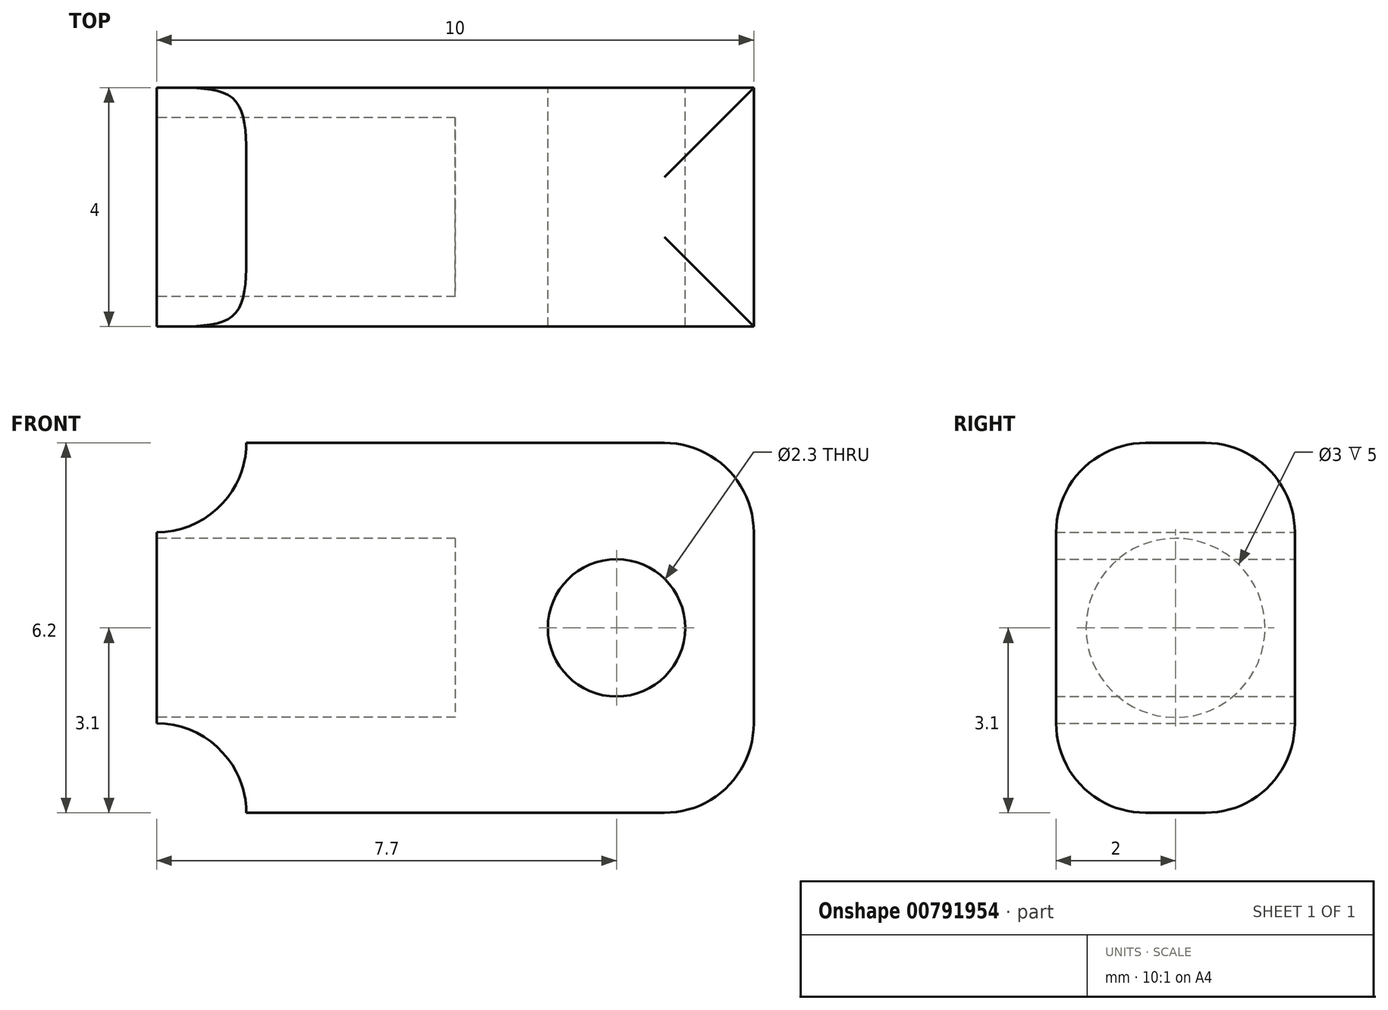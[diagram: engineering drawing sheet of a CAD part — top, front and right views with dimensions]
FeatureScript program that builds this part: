
annotation { "Feature Type Name" : "Feature", "Feature Type Description" : "" }
export const myFeature = defineFeature(function(context is Context, id is Id, definition is map)
    precondition{}
    {
        {
            var Q0;
            Q0=qCreatedBy(makeId("Front.planeOp"),FACE);
            var sketch = newSketch(context, id + "F0", { "sketchPlane" : qUnion([Q0])});
            skLineSegment(sketch, "E0.bottom", {"start": v(5, 3.1) * mm, "end": v(-3.5, 3.1) * mm});
            skLineSegment(sketch, "E0.top", {"start": v(5, -3.1) * mm, "end": v(-3.5, -3.1) * mm});
            skLineSegment(sketch, "E0.left", {"start": v(5, 3.1) * mm, "end": v(5, -3.1) * mm});
            skLineSegment(sketch, "E0.right", {"start": v(-5, 1.6) * mm, "end": v(-5, -1.6) * mm});
            skPoint(sketch, "E0.middle", {"position": v(0, 0) * mm});
            skArc(sketch, "E1", {"start": v(-5, 1.6) * mm, "mid": v(-3.94, 2.04) * mm, "end": v(-3.5, 3.1) * mm});
            skArc(sketch, "E2.MirrorCS", {"start": v(-5, -1.6) * mm, "mid": v(-3.94, -2.04) * mm, "end": v(-3.5, -3.1) * mm});
            skCircle(sketch, "E3", {"center": v(2.7, 0) * mm, "radius": 1.15 * mm});
            skSolve(sketch);
        }
        {
            var Q0;
            Q0 = qSketchRegion(id + "F0", true);
            extrude(context, id + "F1", {"entities" : qUnion([Q0]), "depth" : 4 * mm, "offsetDistance" : 25 * mm});
        }
        {
            var Q0;
            Q0=makeQuery(id+"F1.opExtrude","SWEPT_FACE",FACE,{"disambiguationData":[OSD([sQuery(id+"F0.wireOp",EDGE,"E0.right")])]});
            var sketch = newSketch(context, id + "F2", { "sketchPlane" : qUnion([Q0])});
            skCircle(sketch, "E4", {"center": v(2, 0) * mm, "radius": 1.5 * mm});
            skPoint(sketch, "E4.centerSnap0", {"position": v(2, 1.6) * mm});
            skSolve(sketch);
        }
        {
            var Q0;
            Q0 = qSketchRegion(id + "F2", true);
            extrude(context, id + "F3", {"entities" : qUnion([Q0]), "operationType" : NewBodyOperationType.REMOVE, "oppositeDirection" : true, "depth" : 5 * mm, "offsetDistance" : 25 * mm});
        }
        {
            var Q0;
            Q0=makeQuery(id+"F1.opExtrude","CAP_EDGE",EDGE,{"disambiguationData":[OSD([sQuery(id+"F0.wireOp",EDGE,"E0.bottom")])],"isStart":false});
            var Q1;
            Q1=makeQuery(id+"F1.opExtrude","CAP_EDGE",EDGE,{"disambiguationData":[OSD([sQuery(id+"F0.wireOp",EDGE,"E0.bottom")])],"isStart":true});
            var Q2;
            Q2=makeQuery(id+"F1.opExtrude","CAP_EDGE",EDGE,{"disambiguationData":[OSD([sQuery(id+"F0.wireOp",EDGE,"E0.top")])],"isStart":true});
            var Q3;
            Q3=makeQuery(id+"F1.opExtrude","CAP_EDGE",EDGE,{"disambiguationData":[OSD([sQuery(id+"F0.wireOp",EDGE,"E0.top")])],"isStart":false});
            var Q4;
            Q4=makeQuery(id+"F1.opExtrude","SWEPT_EDGE",EDGE,{"disambiguationData":[OSD([sQuery(id+"F0.wireOp",EDGE,"E0.top"),sQuery(id+"F0.wireOp",EDGE,"E0.left")])]});
            var Q5;
            Q5=makeQuery(id+"F1.opExtrude","SWEPT_EDGE",EDGE,{"disambiguationData":[OSD([sQuery(id+"F0.wireOp",EDGE,"E0.bottom"),sQuery(id+"F0.wireOp",EDGE,"E0.left")])]});
            fillet(context, id + "F4", {"entities" : qUnion([Q0, Q1, Q2, Q3, Q4, Q5]), "radius" : 1.5 * mm, "tangentPropagation" : true, "allowEdgeOverflow" : false});
        }
    });
